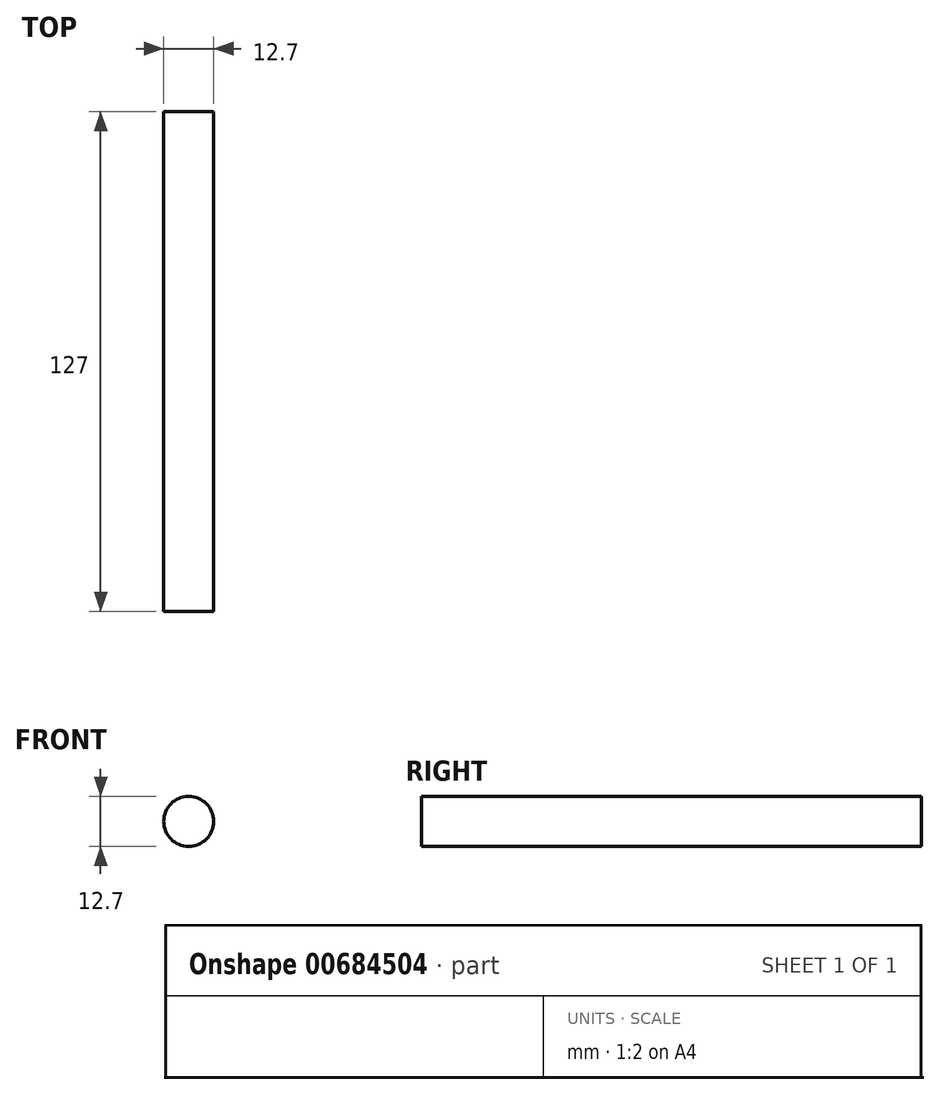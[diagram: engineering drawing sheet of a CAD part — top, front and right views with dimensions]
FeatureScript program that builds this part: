
annotation { "Feature Type Name" : "Feature", "Feature Type Description" : "" }
export const myFeature = defineFeature(function(context is Context, id is Id, definition is map)
    precondition{}
    {
        {
            var Q0;
            Q0=qCreatedBy(makeId("Front.planeOp"),FACE);
            var sketch = newSketch(context, id + "F0", { "sketchPlane" : qUnion([Q0])});
            skCircle(sketch, "E0", {"center": v(0, 0) * mm, "radius": 6.35 * mm});
            skSolve(sketch);
        }
        {
            var Q0;
            Q0 = qSketchRegion(id + "F0", true);
            extrude(context, id + "F1", {"entities" : qUnion([Q0]), "depth" : 127 * mm, "offsetDistance" : 25.4 * mm});
        }
    });
